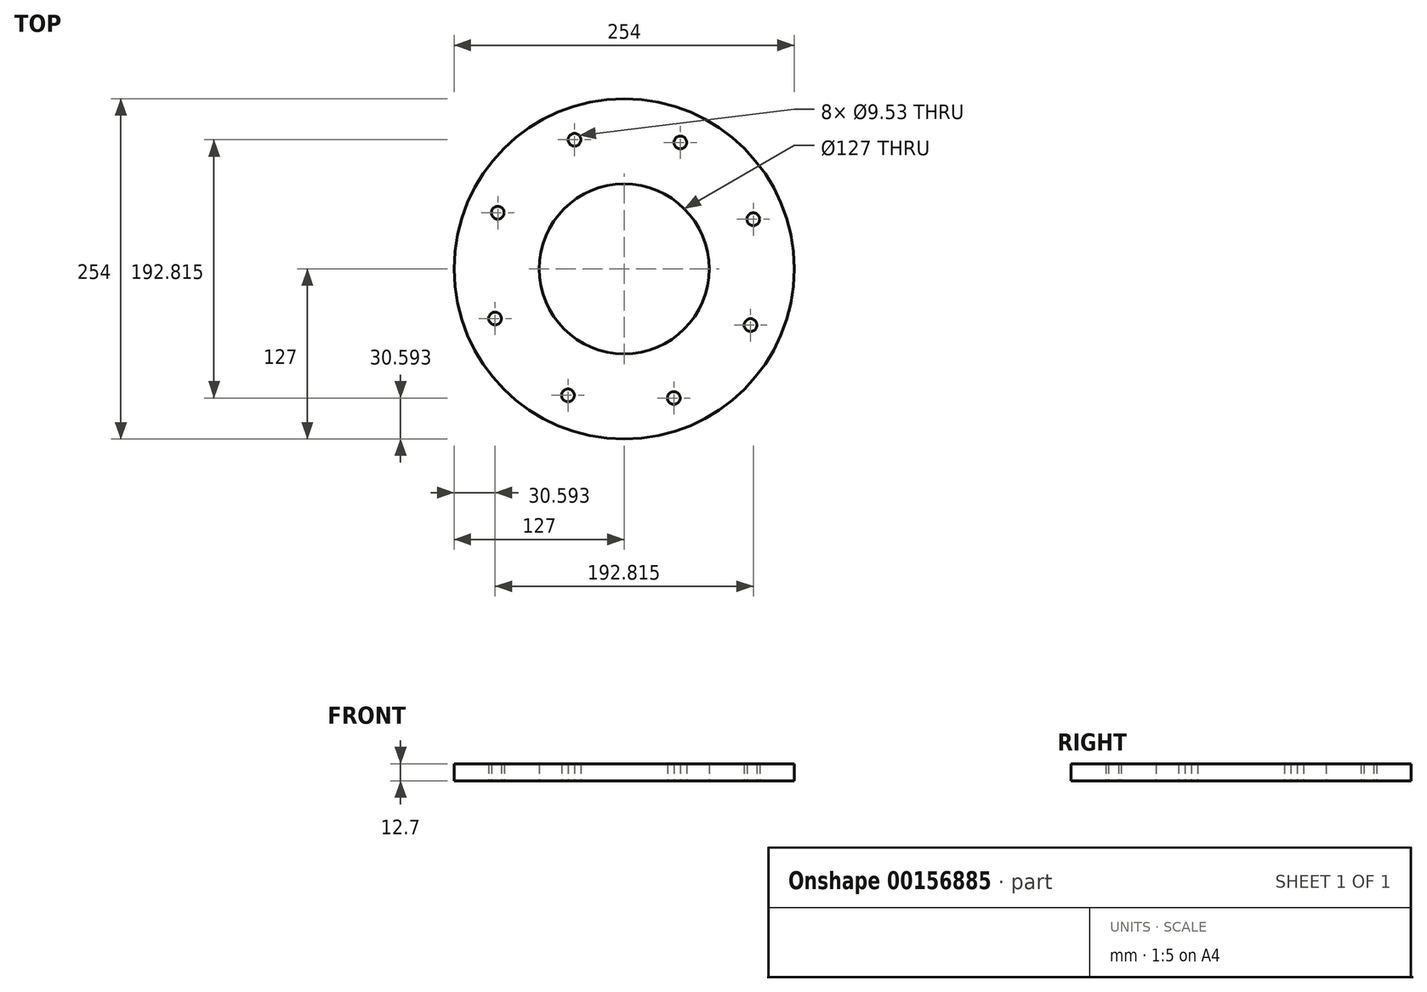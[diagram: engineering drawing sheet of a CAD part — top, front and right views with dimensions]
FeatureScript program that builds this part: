
annotation { "Feature Type Name" : "Feature", "Feature Type Description" : "" }
export const myFeature = defineFeature(function(context is Context, id is Id, definition is map)
    precondition{}
    {
        {
            var Q0;
            Q0=qCreatedBy(makeId("Top.planeOp"),FACE);
            var sketch = newSketch(context, id + "F0", { "sketchPlane" : qUnion([Q0])});
            skCircle(sketch, "E0", {"center": v(0, 0) * mm, "radius": 127 * mm});
            skCircle(sketch, "E1", {"center": v(0, 0) * mm, "radius": 63.5 * mm});
            skCircle(sketch, "E2", {"center": v(-96.4, -37.07) * mm, "radius": 4.76 * mm});
            skCircle(sketch, "E3.1.0", {"center": v(-41.95, -94.39) * mm, "radius": 4.76 * mm});
            skCircle(sketch, "E3.2.0", {"center": v(37.07, -96.4) * mm, "radius": 4.76 * mm});
            skCircle(sketch, "E4.1.3.0", {"center": v(94.39, -41.95) * mm, "radius": 4.76 * mm});
            skCircle(sketch, "E4.1.4.0", {"center": v(96.4, 37.07) * mm, "radius": 4.76 * mm});
            skCircle(sketch, "E4.1.5.0", {"center": v(41.95, 94.39) * mm, "radius": 4.76 * mm});
            skCircle(sketch, "E4.1.6.0", {"center": v(-37.07, 96.4) * mm, "radius": 4.76 * mm});
            skCircle(sketch, "E4.1.7.0", {"center": v(-94.39, 41.95) * mm, "radius": 4.76 * mm});
            skSolve(sketch);
        }
        {
            var Q0;
            Q0=makeQuery(id+"F0.imprint","IMPRINT",FACE,{"disambiguationData":[TD([[makeQuery(id+"F0.imprint","IMPRINT",EDGE,{"derivedFrom":sQuery(id+"F0.wireOp",EDGE,"E0")}),1.0]])]});
            extrude(context, id + "F1", {"entities" : qUnion([Q0]), "depth" : 12.7 * mm});
        }
    });
